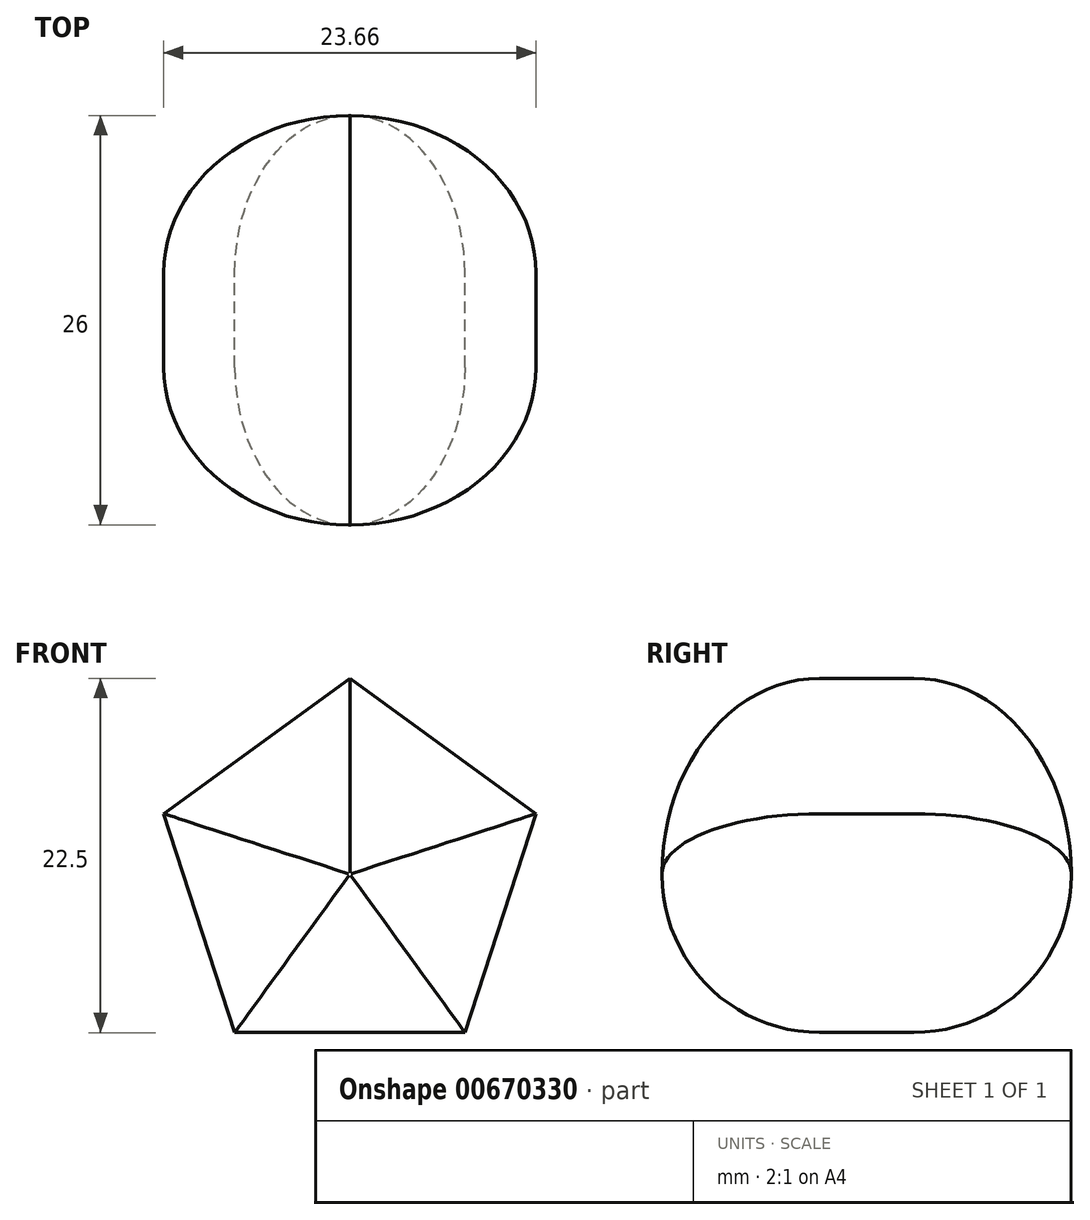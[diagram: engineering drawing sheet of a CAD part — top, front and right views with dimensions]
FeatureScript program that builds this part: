
annotation { "Feature Type Name" : "Feature", "Feature Type Description" : "" }
export const myFeature = defineFeature(function(context is Context, id is Id, definition is map)
    precondition{}
    {
        {
            var Q0;
            Q0=qCreatedBy(makeId("Front.planeOp"),FACE);
            var sketch = newSketch(context, id + "F0", { "sketchPlane" : qUnion([Q0])});
            skCircle(sketch, "E0.cCircle", {"center": v(-46.69, -14.01) * mm, "radius": 10.06 * mm, "construction": true});
            skLineSegment(sketch, "E0.0", {"start": v(-39.38, -24.08) * mm, "end": v(-54, -24.08) * mm});
            skLineSegment(sketch, "E0.1", {"start": v(-54, -24.08) * mm, "end": v(-58.52, -10.17) * mm});
            skLineSegment(sketch, "E0.2", {"start": v(-58.52, -10.17) * mm, "end": v(-46.69, -1.58) * mm});
            skLineSegment(sketch, "E0.3", {"start": v(-46.69, -1.58) * mm, "end": v(-34.86, -10.17) * mm});
            skLineSegment(sketch, "E0.4", {"start": v(-34.86, -10.17) * mm, "end": v(-39.38, -24.08) * mm});
            skPoint(sketch, "E0.0.midPoint", {"position": v(-46.69, -24.08) * mm});
            skSolve(sketch);
        }
        {
            var Q0;
            Q0 = qSketchRegion(id + "F0", true);
            extrude(context, id + "F1", {"entities" : qUnion([Q0]), "depth" : 13 * mm, "offsetDistance" : 25 * mm, "hasSecondDirection" : true, "secondDirectionOppositeDirection" : true, "secondDirectionDepth" : 13 * mm});
        }
        {
            var Q0;
            Q0=makeQuery(id+"F1.opExtrude","CAP_FACE",FACE,{"disambiguationData":[OSD([sQuery(id+"F0.wireOp",EDGE,"E0.0"),sQuery(id+"F0.wireOp",EDGE,"E0.1"),sQuery(id+"F0.wireOp",EDGE,"E0.2"),sQuery(id+"F0.wireOp",EDGE,"E0.3"),sQuery(id+"F0.wireOp",EDGE,"E0.4")])],"isStart":false});
            var Q1;
            Q1=makeQuery(id+"F1.opExtrude","CAP_FACE",FACE,{"disambiguationData":[OSD([sQuery(id+"F0.wireOp",EDGE,"E0.0"),sQuery(id+"F0.wireOp",EDGE,"E0.1"),sQuery(id+"F0.wireOp",EDGE,"E0.2"),sQuery(id+"F0.wireOp",EDGE,"E0.3"),sQuery(id+"F0.wireOp",EDGE,"E0.4")])],"isStart":true});
            fillet(context, id + "F2", {"entities" : qUnion([Q0, Q1]), "radius" : 10 * mm, "tangentPropagation" : true, "allowEdgeOverflow" : false});
        }
    });
